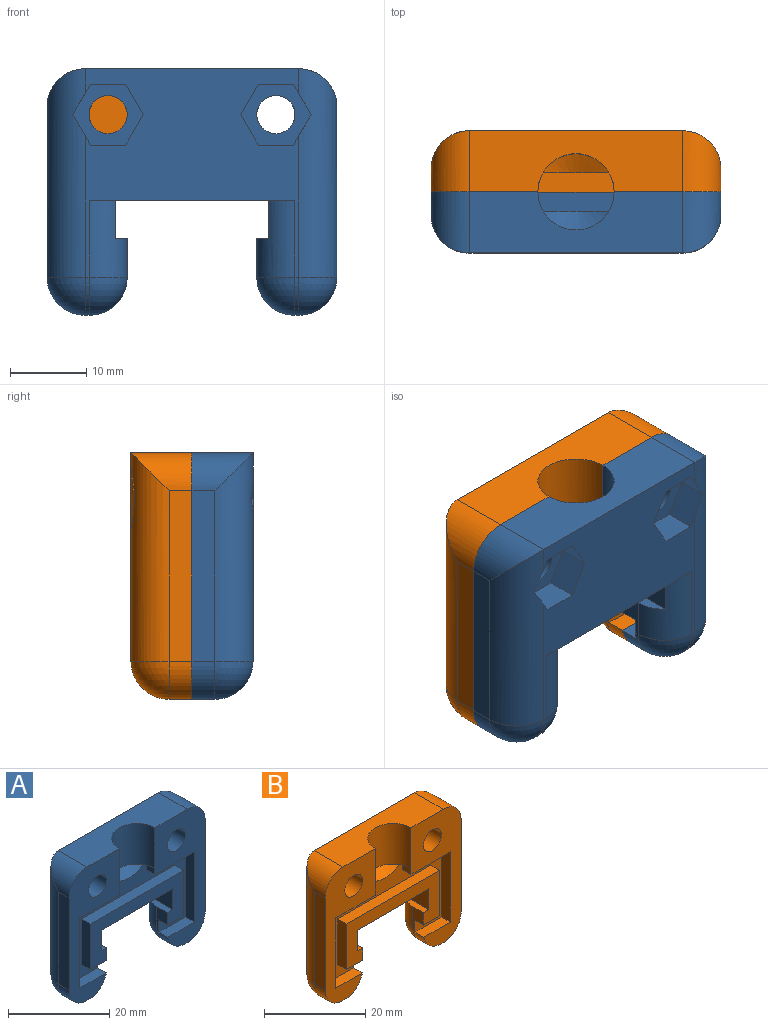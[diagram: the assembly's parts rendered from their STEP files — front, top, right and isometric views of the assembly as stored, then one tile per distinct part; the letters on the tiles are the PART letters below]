
ASSEMBLY  parts=2 mates=1
PART A: 66 faces, bbox 38x8x32.3 mm
  f0: cylinder r=2.5mm len=5mm, axis (0,-1,0), area 62.8mm2, adj f2,f45
  f1: cylinder r=2.5mm len=5mm, axis (0,-1,0), area 62.8mm2, adj f3,f38
  f2: plane 32.31x14mm, normal (0,-1,0), area 215.6mm2, adj f0,f7,f8,f16,f20,f21,f22,f23
  f3: plane 32.31x14mm, normal (0,-1,0), area 215.6mm2, adj f1,f14,f15,f16,f29,f30,f31,f32
  f4: plane 2.5x0.67mm, normal (0,0,-1), area 0.5mm2, adj f32,f33,f35
  f5: plane 5x3mm, normal (1,0,0), area 10mm2, adj f9,f17,f24,f33,f37,f53
  f6: plane 5x3mm, normal (-1,0,0), area 10mm2, adj f13,f17,f28,f33,f36,f65
  f7: plane 22.31x3mm, normal (-1,0,0), area 66.9mm2, adj f2,f52,f54,f55
  f8: plane 3x0.5mm, normal (0,0,-1), area 1.5mm2, adj f2,f53,f55,f58
  f9: plane 6.57x1.5mm, normal (0,0,1), area 8.2mm2, adj f5,f10,f17,f37
  f10: plane 6.57x5mm, normal (1,0,0), area 32.9mm2, adj f9,f11,f17,f37
  f11: plane 27x8mm, normal (0,0,-1), area 163.1mm2, adj f10,f12,f17,f18,f36,f37
  f12: plane 6.57x5mm, normal (-1,0,0), area 32.9mm2, adj f11,f13,f17,f36
  f13: plane 6.57x1.5mm, normal (0,0,1), area 8.2mm2, adj f6,f12,f17,f36
  f14: plane 3x0.5mm, normal (0,0,-1), area 1.5mm2, adj f3,f60,f63,f65
  f15: plane 22.31x3mm, normal (1,0,0), area 66.9mm2, adj f3,f59,f60,f61
  f16: plane 28x8mm, normal (0,0,1), area 184.7mm2, adj f2,f3,f18,f35,f52,f59
  f17: plane 26x11mm, normal (0,-1,0), area 135mm2, adj f5,f6,f9,f10,f11,f12,f13,f24
  f18: plane 28x27.31mm, normal (0,1,0), area 392.9mm2, adj f11,f16,f36,f37,f39,f40,f41,f42
  f19: plane 2.5x0.67mm, normal (0,0,-1), area 0.5mm2, adj f20,f33,f35
  f20: plane 2.5x1.5mm, normal (1,0,0), area 3.7mm2, adj f2,f19,f21,f33
  f21: plane 11x2.5mm, normal (0,0,-1), area 27.5mm2, adj f2,f20,f22,f33
  f22: plane 17x2.5mm, normal (1,0,0), area 42.5mm2, adj f2,f21,f23,f33
  f23: plane 7.4x2.5mm, normal (0,0,1), area 18.5mm2, adj f2,f22,f33,f53
  f24: plane 4.5x2.5mm, normal (0,0,-1), area 11.3mm2, adj f5,f17,f25,f33
  f25: plane 11x2.5mm, normal (-1,0,0), area 27.5mm2, adj f17,f24,f26,f33
  f26: plane 26x2.5mm, normal (0,0,1), area 65mm2, adj f17,f25,f27,f33
  f27: plane 11x2.5mm, normal (1,0,0), area 27.5mm2, adj f17,f26,f28,f33
  f28: plane 4.5x2.5mm, normal (0,0,-1), area 11.3mm2, adj f6,f17,f27,f33
  f29: plane 7.4x2.5mm, normal (0,0,1), area 18.5mm2, adj f3,f30,f33,f65
  f30: plane 17x2.5mm, normal (-1,0,0), area 42.5mm2, adj f3,f29,f31,f33
  f31: plane 11x2.5mm, normal (0,0,-1), area 27.5mm2, adj f3,f30,f32,f33
  f32: plane 2.5x1.5mm, normal (-1,0,0), area 3.7mm2, adj f3,f4,f31,f33
  f33: plane 32x18.5mm, normal (0,-1,0), area 215.5mm2, adj f4,f5,f6,f19,f20,f21,f22,f23
  f34: cone r=0mm half-angle=64.5deg, axis (0,0,1), area 17mm2, adj f33,f35
  f35: cylinder r=5mm len=10mm, axis (0,0,-1), area 154.1mm2, adj f2,f3,f4,f16,f19,f34
  f36: cylinder r=5mm len=10mm, axis (0,0,-1), area 58.7mm2, adj f6,f11,f12,f13,f18,f64
  f37: cylinder r=5mm len=10mm, axis (0,0,1), area 58.7mm2, adj f5,f9,f10,f11,f18,f56
  f38: plane 9.24x8mm, normal (0,1,0), area 35.8mm2, adj f1,f39,f40,f41,f42,f43,f44
  f39: plane 4.04x4.04mm, normal (-0.87,0,0.5), area 18.2mm2, adj f18,f38,f40,f44,f61
  f40: plane 4.62x4mm, normal (0,0,1), area 18.5mm2, adj f18,f38,f39,f41
  f41: plane 4x4mm, normal (0.87,0,0.5), area 18.5mm2, adj f18,f38,f40,f42
  f42: plane 4x4mm, normal (0.87,0,-0.5), area 18.5mm2, adj f18,f38,f41,f43
  f43: plane 4.62x4mm, normal (0,0,-1), area 18.5mm2, adj f18,f38,f42,f44
  f44: plane 4.04x4.04mm, normal (-0.87,0,-0.5), area 18.2mm2, adj f18,f38,f39,f43,f61
  f45: plane 9.24x8mm, normal (0,1,0), area 35.8mm2, adj f0,f46,f47,f48,f49,f50,f51
  f46: plane 4x4mm, normal (-0.87,0,0.5), area 18.5mm2, adj f18,f45,f47,f51
  f47: plane 4.62x4mm, normal (0,0,1), area 18.5mm2, adj f18,f45,f46,f48
  f48: plane 4.04x4.04mm, normal (0.87,0,0.5), area 18.2mm2, adj f18,f45,f47,f49,f54
  f49: plane 4.04x4.04mm, normal (0.87,0,-0.5), area 18.2mm2, adj f18,f45,f48,f50,f54
  f50: plane 4.62x4mm, normal (0,0,-1), area 18.5mm2, adj f18,f45,f49,f51
  f51: plane 4x4mm, normal (-0.87,0,-0.5), area 18.5mm2, adj f18,f45,f46,f50
  f52: cylinder r=5mm len=8mm, axis (0,1,0), area 48.6mm2, adj f2,f7,f16,f54
  f53: cylinder r=5mm len=5mm, axis (0,1,0), area 21mm2, adj f2,f5,f8,f23,f33,f56
  f54: cylinder r=5mm len=27.31mm, axis (0,0,-1), area 195.6mm2, adj f7,f18,f48,f49,f52,f57
  f55: cylinder r=5mm len=5mm, axis (0,1,0), area 23.6mm2, adj f2,f7,f8,f57
  f56: sphere r=5mm, area 39.3mm2, adj f37,f53,f58
  f57: sphere r=5mm, area 39.3mm2, adj f54,f55,f58
  f58: cylinder r=5mm len=5mm, axis (1,0,0), area 3.9mm2, adj f8,f18,f56,f57
  f59: cylinder r=5mm len=8mm, axis (0,1,0), area 48.6mm2, adj f3,f15,f16,f61
  f60: cylinder r=5mm len=5mm, axis (0,1,0), area 23.6mm2, adj f3,f14,f15,f62
  f61: cylinder r=5mm len=27.31mm, axis (0,0,1), area 195.6mm2, adj f15,f18,f39,f44,f59,f62
  f62: sphere r=5mm, area 39.3mm2, adj f60,f61,f63
  f63: cylinder r=5mm len=5mm, axis (1,0,0), area 3.9mm2, adj f14,f18,f62,f64
  f64: sphere r=5mm, area 39.3mm2, adj f36,f63,f65
  f65: cylinder r=5mm len=5mm, axis (0,1,0), area 21mm2, adj f3,f6,f14,f29,f33,f64
PART B: 54 faces, bbox 38x8x32.3 mm
  f0: plane 32.31x14mm, normal (0,-1,0), area 215.6mm2, adj f5,f6,f14,f18,f19,f20,f21,f32
  f1: plane 32.31x14mm, normal (0,-1,0), area 215.6mm2, adj f12,f13,f14,f27,f28,f29,f30,f33
  f2: plane 2.5x0.67mm, normal (0,0,-1), area 0.5mm2, adj f30,f31,f35
  f3: plane 5x3mm, normal (1,0,0), area 10mm2, adj f7,f15,f22,f31,f37,f46
  f4: plane 5x3mm, normal (-1,0,0), area 10mm2, adj f11,f15,f26,f31,f36,f53
  f5: plane 22.31x3mm, normal (-1,0,0), area 66.9mm2, adj f0,f40,f41,f42
  f6: plane 3x0.5mm, normal (0,0,-1), area 1.5mm2, adj f0,f42,f44,f46
  f7: plane 6.57x1.5mm, normal (0,0,1), area 8.2mm2, adj f3,f8,f15,f37
  f8: plane 6.57x5mm, normal (1,0,0), area 32.9mm2, adj f7,f9,f15,f37
  f9: plane 27x8mm, normal (0,0,-1), area 163.1mm2, adj f8,f10,f15,f16,f36,f37
  f10: plane 6.57x5mm, normal (-1,0,0), area 32.9mm2, adj f9,f11,f15,f36
  f11: plane 6.57x1.5mm, normal (0,0,1), area 8.2mm2, adj f4,f10,f15,f36
  f12: plane 3x0.5mm, normal (0,0,-1), area 1.5mm2, adj f1,f48,f51,f53
  f13: plane 22.31x3mm, normal (1,0,0), area 66.9mm2, adj f1,f47,f48,f49
  f14: plane 28x8mm, normal (0,0,1), area 184.7mm2, adj f0,f1,f16,f35,f40,f47
  f15: plane 26x11mm, normal (0,-1,0), area 135mm2, adj f3,f4,f7,f8,f9,f10,f11,f22
  f16: plane 28x27.31mm, normal (0,1,0), area 337.1mm2, adj f9,f14,f36,f37,f38,f39,f41,f44
  f17: plane 2.5x0.67mm, normal (0,0,-1), area 0.5mm2, adj f18,f31,f35
  f18: plane 2.5x1.5mm, normal (1,0,0), area 3.7mm2, adj f0,f17,f19,f31
  f19: plane 11x2.5mm, normal (0,0,-1), area 27.5mm2, adj f0,f18,f20,f31
  f20: plane 17x2.5mm, normal (1,0,0), area 42.5mm2, adj f0,f19,f21,f31
  f21: plane 7.4x2.5mm, normal (0,0,1), area 18.5mm2, adj f0,f20,f31,f46
  f22: plane 4.5x2.5mm, normal (0,0,-1), area 11.3mm2, adj f3,f15,f23,f31
  f23: plane 11x2.5mm, normal (-1,0,0), area 27.5mm2, adj f15,f22,f24,f31
  f24: plane 26x2.5mm, normal (0,0,1), area 65mm2, adj f15,f23,f25,f31
  f25: plane 11x2.5mm, normal (1,0,0), area 27.5mm2, adj f15,f24,f26,f31
  f26: plane 4.5x2.5mm, normal (0,0,-1), area 11.3mm2, adj f4,f15,f25,f31
  f27: plane 7.4x2.5mm, normal (0,0,1), area 18.5mm2, adj f1,f28,f31,f53
  f28: plane 17x2.5mm, normal (-1,0,0), area 42.5mm2, adj f1,f27,f29,f31
  f29: plane 11x2.5mm, normal (0,0,-1), area 27.5mm2, adj f1,f28,f30,f31
  f30: plane 2.5x1.5mm, normal (-1,0,0), area 3.7mm2, adj f1,f2,f29,f31
  f31: plane 32x18.5mm, normal (0,-1,0), area 215.5mm2, adj f2,f3,f4,f17,f18,f19,f20,f21
  f32: cylinder r=2.5mm len=5mm, axis (0,-1,0), area 78.5mm2, adj f0,f38
  f33: cylinder r=2.5mm len=5mm, axis (0,-1,0), area 78.5mm2, adj f1,f39
  f34: cone r=0mm half-angle=64.5deg, axis (0,0,1), area 17mm2, adj f31,f35
  f35: cylinder r=5mm len=10mm, axis (0,0,-1), area 154.1mm2, adj f0,f1,f2,f14,f17,f34
  f36: cylinder r=5mm len=10mm, axis (0,0,-1), area 58.7mm2, adj f4,f9,f10,f11,f16,f52
  f37: cylinder r=5mm len=10mm, axis (0,0,1), area 58.7mm2, adj f3,f7,f8,f9,f16,f45
  f38: cone r=5.5mm half-angle=45deg, axis (0,1,0), area 103mm2, adj f16,f32,f41
  f39: cone r=5.5mm half-angle=45deg, axis (0,1,0), area 103mm2, adj f16,f33,f49
  f40: cylinder r=5mm len=8mm, axis (0,1,0), area 48.6mm2, adj f0,f5,f14,f41
  f41: cylinder r=5mm len=27.31mm, axis (0,0,-1), area 186.3mm2, adj f5,f16,f38,f40,f43
  f42: cylinder r=5mm len=5mm, axis (0,1,0), area 23.6mm2, adj f0,f5,f6,f43
  f43: sphere r=5mm, area 39.3mm2, adj f41,f42,f44
  f44: cylinder r=5mm len=5mm, axis (1,0,0), area 3.9mm2, adj f6,f16,f43,f45
  f45: sphere r=5mm, area 39.3mm2, adj f37,f44,f46
  f46: cylinder r=5mm len=5mm, axis (0,1,0), area 21mm2, adj f0,f3,f6,f21,f31,f45
  f47: cylinder r=5mm len=8mm, axis (0,1,0), area 48.6mm2, adj f1,f13,f14,f49
  f48: cylinder r=5mm len=5mm, axis (0,1,0), area 23.6mm2, adj f1,f12,f13,f50
  f49: cylinder r=5mm len=27.31mm, axis (0,0,1), area 186.3mm2, adj f13,f16,f39,f47,f50
  f50: sphere r=5mm, area 39.3mm2, adj f48,f49,f51
  f51: cylinder r=5mm len=5mm, axis (1,0,0), area 3.9mm2, adj f12,f16,f50,f52
  f52: sphere r=5mm, area 39.3mm2, adj f36,f51,f53
  f53: cylinder r=5mm len=5mm, axis (0,1,0), area 21mm2, adj f1,f4,f12,f27,f31,f52
PLACE A rot(axis=(0,0,1),180deg) t=(20.06,-16.76,7.89)mm
PLACE B rot(axis=(1,0,0),0deg) t=(-17.94,-0.76,7.89)mm
MATE fastened A.f0 <-> B.f33  axis (0,1,0) through (12.06,-8.76,34.2)mm
